# Revit family: Robot Cook (a)
name_source: partatom
category: Equipement spécialisé
revit_build: Autodesk Revit LT 2015 (Build: 20140606_1530(x64)
units: mm (PartAtom-declared; Revit-internal decimal feet)

## types (3) — shared parameters
Apparent Power = 0 VA
Cycle = 50 Hz
Depth = 320 mm  [stored 1.04987 ft]
Description = ROBOT COOK
Fabricant = ROBOT COUPE
Height = 525 mm
Modèle = Robot Cook
Phase = 1
Speeds (Rpm) = 100 to 3500
URL = www.robot-coupe.com
Watts = 1800 W
Weight = 15 kg
Width = 231 mm
Width Electrique connexion = 80 mm  [stored 0.262467 ft]
water = Connector
zero-valued in all types: Cold water supply, Cold water supply height, Used water, Waste water height

## per-type parameters (varying)
| type | Amps | Volts |
| Robot Cook  230/50/1 | 8 A | 230 V |
| Robot Cook  220-240/50-60/1 | 8 A | 220 V |
| Robot Cook  100-120/50-60/1 | 15 A | 100 V |

note: [stored X ft] marks values corroborated as IEEE doubles in the binary element streams (Revit-internal decimal feet)

## geometry (parser evidence)
native form markers: Blend x104, Sweep x5
no freeform markers — native parametric forms only
